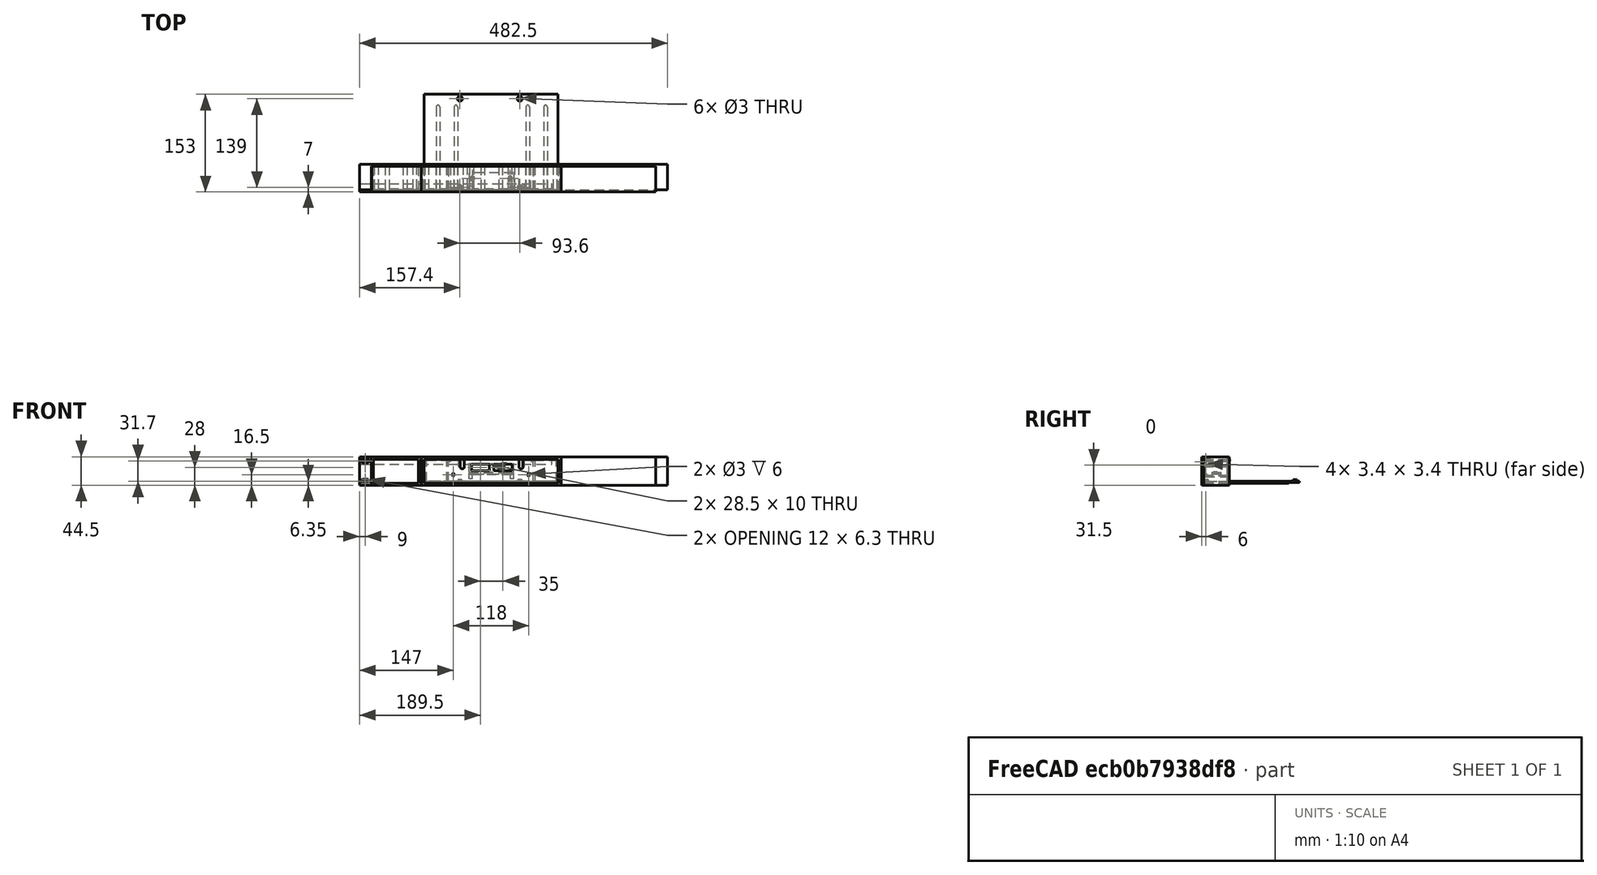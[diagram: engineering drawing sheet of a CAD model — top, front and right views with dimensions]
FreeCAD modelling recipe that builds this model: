
FCSTD DOCUMENT  (FreeCAD 0.19R24291 (Git))
Label: Rack_-_Middle_wider
License: All rights reserved
LicenseURL: http://en.wikipedia.org/wiki/All_rights_reserved
objects: Part::Box×100, Part::MultiFuse×44, Part::Cut×30, Part::Fillet×18, Part::Cylinder×18, Part::Cone×8, Mesh::Feature×7, Part::MultiCommon×6, App::MeasureDistance×1
note: 224 computed .brp shape members not serialized (recipe doc carries the construction recipe); baked Part::Feature solids carry a one-line shape summary decoded from their .brp

FEATURE [Mesh::Feature] Rack___Right_Side  label="Rack - Right Side"
FEATURE [Mesh::Feature] Rack___Middle  label="Rack - Middle"
FEATURE [Mesh::Feature] Rack___Left_Side  label="Rack - Left Side"
FEATURE [Part::Box] Box  label="Cube"
  AttacherType = Attacher::AttachEngine3D
  Height = 10
  Length = 300
  Placement = pos=(1,0,33) rot=(0,0,1;0rad)
  Width = 10
FEATURE [Part::Box] Box001  label="Cube001"
  AttacherType = Attacher::AttachEngine3D
  Height = 44.5
  Length = 445
  Placement = pos=(18.75,-3,0) rot=(0,0,1;0rad)
  Width = 40
FEATURE [Part::Box] Box002  label="Cube002"
  AttacherType = Attacher::AttachEngine3D
  Height = 44.5
  Length = 219.5
  Placement = pos=(96.5,-3,0) rot=(0,0,1;0rad)
  Width = 40
FEATURE [Part::Box] Box003  label="Cube003"
  AttacherType = Attacher::AttachEngine3D
  Height = 44
  Length = 482.5
  Width = 40
FEATURE [Part::Box] Box004  label="Cube004"
  AttacherType = Attacher::AttachEngine3D
  Height = 17.92
  Length = 3
  Placement = pos=(313.75,0,13.25) rot=(0,0,1;0rad)
  Width = 37
FEATURE [Part::Box] Box005  label="Cube005"
  AttacherType = Attacher::AttachEngine3D
  Height = 17.92
  Length = 3
  Placement = pos=(313,0,12.75) rot=(0,1,0;0.959931rad)
  Width = 37
FEATURE [Part::Box] Box006  label="Cube006"
  AttacherType = Attacher::AttachEngine3D
  Height = 17.92
  Length = 3
  Placement = pos=(313,0,35.35) rot=(0,1,0;2.18166rad)
  Width = 37
FEATURE [Part::MultiFuse] Fusion
  Shapes = -> [Box006,Box005]
FEATURE [Part::Cut] Cut
  Base = -> Box004
  Tool = -> Fusion
FEATURE [Part::Box] Box007  label="Cube007"
  AttacherType = Attacher::AttachEngine3D
  Height = 17.92
  Length = 3
  Placement = pos=(314.75,-3,13.25) rot=(0,0,1;0.785398rad)
  Width = 37
FEATURE [Part::Cut] Cut001
  Base = -> Cut
  Tool = -> Box007
FEATURE [Part::Cut] Cut002
  Base = -> Box002
  Tool = -> Cut001
FEATURE [Part::Box] Box008  label="Cube008"
  AttacherType = Attacher::AttachEngine3D
  Height = 17.92
  Length = 3
  Placement = pos=(313,0,12.75) rot=(0,1,0;0.959931rad)
  Width = 37
FEATURE [Part::Box] Box009  label="Cube009"
  AttacherType = Attacher::AttachEngine3D
  Height = 17.92
  Length = 3
  Placement = pos=(313,0,35.35) rot=(0,1,0;2.18166rad)
  Width = 37
FEATURE [Part::MultiFuse] Fusion001
  Shapes = -> [Box009,Box008]
FEATURE [Part::Box] Box010  label="Cube010"
  AttacherType = Attacher::AttachEngine3D
  Height = 17.92
  Length = 3
  Placement = pos=(314.75,-3,13.25) rot=(0,0,1;0.785398rad)
  Width = 37
FEATURE [Part::Box] Box011  label="Cube011"
  AttacherType = Attacher::AttachEngine3D
  Height = 17.92
  Length = 3
  Placement = pos=(313.75,0,13.25) rot=(0,0,1;0rad)
  Width = 37
FEATURE [Part::Cut] Cut003
  Base = -> Box011
  Tool = -> Fusion001
FEATURE [Part::Cut] Cut004
  Base = -> Cut003
  Placement = pos=(413.25,0,44.45) rot=(0,1,0;3.14159rad)
  Tool = -> Box010
FEATURE [Part::Cut] Cut005  label="middle"
  Base = -> Cut002
  Tool = -> Cut004
FEATURE [Part::Box] Box012  label="Cube012"
  AttacherType = Attacher::AttachEngine3D
  Height = 17.92
  Length = 3
  Placement = pos=(313.75,0,13.25) rot=(0,0,1;0rad)
  Width = 37
FEATURE [Part::Box] Box013  label="Cube013"
  AttacherType = Attacher::AttachEngine3D
  Height = 17.92
  Length = 3
  Placement = pos=(314.75,-3,13.25) rot=(0,0,1;0.785398rad)
  Width = 37
FEATURE [Part::Box] Box014  label="Cube014"
  AttacherType = Attacher::AttachEngine3D
  Height = 17.92
  Length = 3
  Placement = pos=(313,0,12.75) rot=(0,1,0;0.959931rad)
  Width = 37
FEATURE [Part::Box] Box015  label="Cube015"
  AttacherType = Attacher::AttachEngine3D
  Height = 17.92
  Length = 3
  Placement = pos=(313,0,35.35) rot=(0,1,0;2.18166rad)
  Width = 37
FEATURE [Part::MultiFuse] Fusion002
  Shapes = -> [Box015,Box014]
FEATURE [Part::Cut] Cut006
  Base = -> Box012
  Tool = -> Fusion002
FEATURE [Part::Cut] Cut007
  Base = -> Cut006
  Placement = pos=(413.25,0,44.45) rot=(0,1,0;3.14159rad)
  Tool = -> Box013
FEATURE [Part::Box] Box016  label="Cube016"
  AttacherType = Attacher::AttachEngine3D
  Height = 44.5
  Length = 96.5
  Placement = pos=(0,-3,0) rot=(0,0,1;0rad)
  Width = 40
FEATURE [Part::MultiFuse] Fusion003
  Shapes = -> [Cut007,Box016]
FEATURE [Part::Box] Box017  label="Cube017"
  AttacherType = Attacher::AttachEngine3D
  Height = 37.95
  Length = 70.5
  Placement = pos=(22,-4,2.75) rot=(0,0,1;0rad)
  Width = 45
FEATURE [Part::Cut] Cut008  label="left"
  Base = -> Fusion003
  Tool = -> Box017
FEATURE [Part::Box] Box018  label="Cube018"
  AttacherType = Attacher::AttachEngine3D
  Height = 45
  Length = 19
  Width = 37
FEATURE [Part::Box] Box019  label="Cube019"
  AttacherType = Attacher::AttachEngine3D
  Height = 6.3
  Length = 12
  Placement = pos=(3,-3,3.2) rot=(0,0,1;0rad)
  Width = 10
FEATURE [Part::Fillet] Fillet
  Base = -> Box019
  Edges = 4 edges r=3: [Edge2,Edge4,Edge6,Edge8]
  Placement = pos=(0,-1,0) rot=(0,0,1;0rad)
FEATURE [Part::Box] Box020  label="Cube020"
  AttacherType = Attacher::AttachEngine3D
  Height = 6.3
  Length = 12
  Placement = pos=(3,-3,3.2) rot=(0,0,1;0rad)
  Width = 10
FEATURE [Part::Fillet] Fillet001
  Base = -> Box020
  Edges = 4 edges r=3: [Edge2,Edge4,Edge6,Edge8]
  Placement = pos=(0,-1,31.7) rot=(0,0,1;0rad)
FEATURE [Part::MultiFuse] Fusion004
  Shapes = -> [Box018,Fillet,Fillet001]
FEATURE [Part::Cut] Cut009
  Base = -> Cut008
  Tool = -> Fusion004
FEATURE [Part::Box] Box021  label="Cube021"
  AttacherType = Attacher::AttachEngine3D
  Height = 4
  Length = 19
  Placement = pos=(22,0,0) rot=(0,0,1;0rad)
  Width = 37
FEATURE [Part::Box] Box022  label="Cube022"
  AttacherType = Attacher::AttachEngine3D
  Height = 4
  Length = 22
  Placement = pos=(47,0,0) rot=(0,0,1;0rad)
  Width = 37
FEATURE [Part::Box] Box023  label="Cube023"
  AttacherType = Attacher::AttachEngine3D
  Height = 4
  Length = 18
  Placement = pos=(75,0,0) rot=(0,0,1;0rad)
  Width = 37
FEATURE [Part::Box] Box024  label="Cube024"
  AttacherType = Attacher::AttachEngine3D
  Height = 4
  Length = 54
  Placement = pos=(30.05,0,39.45) rot=(0,0,1;0rad)
  Width = 37
FEATURE [Part::Box] Box025  label="Cube025"
  AttacherType = Attacher::AttachEngine3D
  Height = 4
  Length = 3
  Placement = pos=(21.05,0,39.45) rot=(0,0,1;0rad)
  Width = 37
FEATURE [Part::Box] Box026  label="Cube026"
  AttacherType = Attacher::AttachEngine3D
  Height = 4
  Length = 4
  Placement = pos=(90.05,0,39.45) rot=(0,0,1;0rad)
  Width = 37
FEATURE [Part::Box] Box027  label="Cube027"
  AttacherType = Attacher::AttachEngine3D
  Height = 10
  Length = 71
  Placement = pos=(22,-3,0) rot=(1,0,0;0.785398rad)
  Width = 10
FEATURE [Part::MultiFuse] Fusion005
  Shapes = -> [Box021,Box022,Box023]
FEATURE [Part::Cut] Cut010
  Base = -> Fusion005
  Tool = -> Box027
FEATURE [Part::MultiFuse] Fusion006
  Shapes = -> [Box024,Box025,Box026]
FEATURE [Part::Box] Box028  label="Cube028"
  AttacherType = Attacher::AttachEngine3D
  Height = 10
  Length = 80
  Placement = pos=(13,-8,35) rot=(1,0,0;-0.785398rad)
  Width = 10
FEATURE [Part::Cut] Cut011
  Base = -> Fusion006
  Tool = -> Box028
FEATURE [Part::MultiFuse] Fusion007  label="Rack - Left Side shorter"
  Shapes = -> [Cut009,Cut010,Cut011]
FEATURE [Part::Box] Box029  label="Cube029"
  AttacherType = Attacher::AttachEngine3D
  Height = 37.95
  Length = 210.4
  Placement = pos=(101,-4,2.75) rot=(0,0,1;0rad)
  Width = 45
FEATURE [Part::Cut] Cut012
  Base = -> Cut005
  Tool = -> Box029
FEATURE [Part::Box] Box030  label="Cube030"
  AttacherType = Attacher::AttachEngine3D
  Height = 4
  Length = 3
  Placement = pos=(21.05,0,39.45) rot=(0,0,1;0rad)
  Width = 37
FEATURE [Part::Box] Box031  label="Cube031"
  AttacherType = Attacher::AttachEngine3D
  Height = 10
  Length = 85
  Placement = pos=(13,-8,35) rot=(-1,0,0;0.785398rad)
  Width = 10
FEATURE [Part::Box] Box032  label="Cube032"
  AttacherType = Attacher::AttachEngine3D
  Height = 4
  Length = 4
  Placement = pos=(90.05,0,39.45) rot=(0,0,1;0rad)
  Width = 37
FEATURE [Part::Box] Box033  label="Cube033"
  AttacherType = Attacher::AttachEngine3D
  Height = 4
  Length = 54
  Placement = pos=(30.05,0,39.45) rot=(0,0,1;0rad)
  Width = 37
FEATURE [Part::MultiFuse] Fusion008
  Shapes = -> [Box033,Box030,Box032]
FEATURE [Part::Cut] Cut013
  Base = -> Fusion008
  Placement = pos=(219.5,0,0) rot=(0,0,1;0rad)
  Tool = -> Box031
FEATURE [Part::Box] Box034  label="Cube034"
  AttacherType = Attacher::AttachEngine3D
  Height = 4
  Length = 4
  Placement = pos=(90.05,0,39.45) rot=(0,0,1;0rad)
  Width = 37
FEATURE [Part::Box] Box035  label="Cube035"
  AttacherType = Attacher::AttachEngine3D
  Height = 10
  Length = 85
  Placement = pos=(13,-8,35) rot=(-1,0,0;0.785398rad)
  Width = 10
FEATURE [Part::Box] Box036  label="Cube036"
  AttacherType = Attacher::AttachEngine3D
  Height = 4
  Length = 54
  Placement = pos=(30.05,0,39.45) rot=(0,0,1;0rad)
  Width = 37
FEATURE [Part::Box] Box037  label="Cube037"
  AttacherType = Attacher::AttachEngine3D
  Height = 4
  Length = 3
  Placement = pos=(21.05,0,39.45) rot=(0,0,1;0rad)
  Width = 37
FEATURE [Part::MultiFuse] Fusion009
  Shapes = -> [Box036,Box037,Box034]
FEATURE [Part::Cut] Cut014
  Base = -> Fusion009
  Placement = pos=(149,0,0) rot=(0,0,1;0rad)
  Tool = -> Box035
FEATURE [Part::Box] Box038  label="Cube038"
  AttacherType = Attacher::AttachEngine3D
  Height = 4
  Length = 4
  Placement = pos=(90.05,0,39.45) rot=(0,0,1;0rad)
  Width = 37
FEATURE [Part::Box] Box039  label="Cube039"
  AttacherType = Attacher::AttachEngine3D
  Height = 10
  Length = 85
  Placement = pos=(13,-8,35) rot=(-1,0,0;0.785398rad)
  Width = 10
FEATURE [Part::Box] Box040  label="Cube040"
  AttacherType = Attacher::AttachEngine3D
  Height = 4
  Length = 54
  Placement = pos=(30.05,0,39.45) rot=(0,0,1;0rad)
  Width = 37
FEATURE [Part::Box] Box041  label="Cube041"
  AttacherType = Attacher::AttachEngine3D
  Height = 4
  Length = 3
  Placement = pos=(21.05,0,39.45) rot=(0,0,1;0rad)
  Width = 37
FEATURE [Part::MultiFuse] Fusion010
  Shapes = -> [Box040,Box041,Box038]
FEATURE [Part::Cut] Cut015
  Base = -> Fusion010
  Placement = pos=(79,0,0) rot=(0,0,1;0rad)
  Tool = -> Box039
FEATURE [Part::Box] Box042  label="Cube042"
  AttacherType = Attacher::AttachEngine3D
  Height = 4
  Length = 18
  Placement = pos=(75,0,0) rot=(0,0,1;0rad)
  Width = 37
FEATURE [Part::Box] Box043  label="Cube043"
  AttacherType = Attacher::AttachEngine3D
  Height = 4
  Length = 19
  Placement = pos=(22,0,0) rot=(0,0,1;0rad)
  Width = 37
FEATURE [Part::Box] Box044  label="Cube044"
  AttacherType = Attacher::AttachEngine3D
  Height = 4
  Length = 22
  Placement = pos=(47,0,0) rot=(0,0,1;0rad)
  Width = 37
FEATURE [Part::MultiFuse] Fusion011
  Shapes = -> [Box043,Box044,Box042]
FEATURE [Part::Box] Box045  label="Cube045"
  AttacherType = Attacher::AttachEngine3D
  Height = 10
  Length = 71
  Placement = pos=(22,-3,0) rot=(1,0,0;0.785398rad)
  Width = 10
FEATURE [Part::Cut] Cut016
  Base = -> Fusion011
  Placement = pos=(219.5,0,0) rot=(0,0,1;0rad)
  Tool = -> Box045
FEATURE [Part::Box] Box046  label="Cube046"
  AttacherType = Attacher::AttachEngine3D
  Height = 4
  Length = 18
  Placement = pos=(75,0,0) rot=(0,0,1;0rad)
  Width = 37
FEATURE [Part::Box] Box047  label="Cube047"
  AttacherType = Attacher::AttachEngine3D
  Height = 4
  Length = 19
  Placement = pos=(22,0,0) rot=(0,0,1;0rad)
  Width = 37
FEATURE [Part::Box] Box048  label="Cube048"
  AttacherType = Attacher::AttachEngine3D
  Height = 4
  Length = 22
  Placement = pos=(47,0,0) rot=(0,0,1;0rad)
  Width = 37
FEATURE [Part::MultiFuse] Fusion012
  Shapes = -> [Box047,Box048,Box046]
FEATURE [Part::Box] Box049  label="Cube049"
  AttacherType = Attacher::AttachEngine3D
  Height = 10
  Length = 71
  Placement = pos=(22,-3,0) rot=(1,0,0;0.785398rad)
  Width = 10
FEATURE [Part::Cut] Cut017
  Base = -> Fusion012
  Placement = pos=(149.5,0,0) rot=(0,0,1;0rad)
  Tool = -> Box049
FEATURE [Part::Box] Box050  label="Cube050"
  AttacherType = Attacher::AttachEngine3D
  Height = 4
  Length = 18
  Placement = pos=(75,0,0) rot=(0,0,1;0rad)
  Width = 37
FEATURE [Part::Box] Box051  label="Cube051"
  AttacherType = Attacher::AttachEngine3D
  Height = 4
  Length = 19
  Placement = pos=(22,0,0) rot=(0,0,1;0rad)
  Width = 37
FEATURE [Part::Box] Box052  label="Cube052"
  AttacherType = Attacher::AttachEngine3D
  Height = 4
  Length = 22
  Placement = pos=(47,0,0) rot=(0,0,1;0rad)
  Width = 37
FEATURE [Part::MultiFuse] Fusion013
  Shapes = -> [Box051,Box052,Box050]
FEATURE [Part::Box] Box053  label="Cube053"
  AttacherType = Attacher::AttachEngine3D
  Height = 10
  Length = 71
  Placement = pos=(22,-3,0) rot=(1,0,0;0.785398rad)
  Width = 10
FEATURE [Part::Cut] Cut018
  Base = -> Fusion013
  Placement = pos=(79,0,0) rot=(0,0,1;0rad)
  Tool = -> Box053
FEATURE [Part::MultiFuse] Fusion014  label="Rack - Middle Wider"
  Shapes = -> [Cut012,Cut013,Cut014,Cut015,Cut016,Cut017,Cut018]
FEATURE [Part::Box] Box054  label="Cube054"
  AttacherType = Attacher::AttachEngine3D
  Height = 2
  Length = 150
  Placement = pos=(0,-56,0) rot=(0,0,1;0rad)
  Width = 209.75
FEATURE [Part::Cylinder] Cylinder
  Angle = 360
  AttacherType = Attacher::AttachEngine3D
  Height = 10
  Placement = pos=(4,4,-1) rot=(0,0,1;0rad)
  Radius = 1.5
FEATURE [Part::Box] Box055  label="Cube055"
  AttacherType = Attacher::AttachEngine3D
  Height = 37.5
  Length = 3
  Placement = pos=(-5,-55,-1) rot=(0,0,1;0rad)
  Width = 209.75
FEATURE [Part::Box] Box056  label="Cube056"
  AttacherType = Attacher::AttachEngine3D
  Height = 3
  Length = 130
  Placement = pos=(0,0,-2) rot=(0,0,1;0rad)
  Width = 5.5
FEATURE [Part::Fillet] Fillet002
  Base = -> Box056
  Edges = 2 edges r=0.5: [Edge9,Edge11]
FEATURE [Part::Cylinder] Cylinder004
  Angle = 360
  AttacherType = Attacher::AttachEngine3D
  Height = 3
  Placement = pos=(130,2.75,-2) rot=(0,0,-1;0rad)
  Radius = 2.75
FEATURE [Part::Fillet] Fillet003
  Base = -> Cylinder004
  Edges = 1 edges r=0.5: [Edge3]
FEATURE [Part::MultiFuse] Fusion015
  Placement = pos=(0,-39.25,1) rot=(0,0,1;0rad)
  Shapes = -> [Fillet002,Fillet003]
FEATURE [Part::Cylinder] Cylinder005
  Angle = 360
  AttacherType = Attacher::AttachEngine3D
  Height = 3
  Placement = pos=(130,2.75,-2) rot=(0,0,-1;0rad)
  Radius = 2.75
FEATURE [Part::Box] Box057  label="Cube057"
  AttacherType = Attacher::AttachEngine3D
  Height = 3
  Length = 130
  Placement = pos=(0,0,-2) rot=(0,0,1;0rad)
  Width = 5.5
FEATURE [Part::Fillet] Fillet004
  Base = -> Box057
  Edges = 2 edges r=0.5: [Edge9,Edge11]
FEATURE [Part::Fillet] Fillet005
  Base = -> Cylinder005
  Edges = 1 edges r=0.5: [Edge3]
FEATURE [Part::MultiFuse] Fusion016
  Placement = pos=(0,129.25,1) rot=(0,0,1;0rad)
  Shapes = -> [Fillet004,Fillet005]
FEATURE [Part::Cylinder] Cylinder006
  Angle = 360
  AttacherType = Attacher::AttachEngine3D
  Height = 3
  Placement = pos=(130,2.75,-2) rot=(0,0,-1;0rad)
  Radius = 2.75
FEATURE [Part::Box] Box058  label="Cube058"
  AttacherType = Attacher::AttachEngine3D
  Height = 3
  Length = 130
  Placement = pos=(0,0,-2) rot=(0,0,1;0rad)
  Width = 5.5
FEATURE [Part::Fillet] Fillet006
  Base = -> Box058
  Edges = 2 edges r=0.5: [Edge9,Edge11]
FEATURE [Part::Fillet] Fillet007
  Base = -> Cylinder006
  Edges = 1 edges r=0.5: [Edge3]
FEATURE [Part::MultiFuse] Fusion017
  Placement = pos=(0,101.25,1) rot=(0,0,1;0rad)
  Shapes = -> [Fillet006,Fillet007]
FEATURE [Part::Cylinder] Cylinder007
  Angle = 360
  AttacherType = Attacher::AttachEngine3D
  Height = 3
  Placement = pos=(130,2.75,-2) rot=(0,0,-1;0rad)
  Radius = 2.75
FEATURE [Part::Box] Box059  label="Cube059"
  AttacherType = Attacher::AttachEngine3D
  Height = 3
  Length = 130
  Placement = pos=(0,0,-2) rot=(0,0,1;0rad)
  Width = 5.5
FEATURE [Part::Fillet] Fillet008
  Base = -> Box059
  Edges = 2 edges r=0.5: [Edge9,Edge11]
FEATURE [Part::Fillet] Fillet009
  Base = -> Cylinder007
  Edges = 1 edges r=0.5: [Edge3]
FEATURE [Part::MultiFuse] Fusion018
  Placement = pos=(0,-11.25,1) rot=(0,0,1;0rad)
  Shapes = -> [Fillet008,Fillet009]
FEATURE [Part::Box] Box060  label="Cube060"
  AttacherType = Attacher::AttachEngine3D
  Height = 35.2
  Length = 40
  Placement = pos=(0,-20,0) rot=(0,0,1;0rad)
  Width = 3
FEATURE [Part::Box] Box061  label="Cube061"
  AttacherType = Attacher::AttachEngine3D
  Height = 35.2
  Length = 40
  Placement = pos=(0,115.5,0) rot=(0,0,1;0rad)
  Width = 3
FEATURE [Part::Cylinder] Cylinder008
  Angle = 360
  AttacherType = Attacher::AttachEngine3D
  Height = 3
  Placement = pos=(38,2.5,-2) rot=(0,0,-1;0rad)
  Radius = 2.5
FEATURE [Part::Box] Box062  label="Cube062"
  AttacherType = Attacher::AttachEngine3D
  Height = 3
  Length = 38
  Placement = pos=(0,0,-2) rot=(0,0,1;0rad)
  Width = 5
FEATURE [Part::Fillet] Fillet010
  Base = -> Box062
  Edges = 2 edges r=0.5: [Edge9,Edge11]
FEATURE [Part::Fillet] Fillet011
  Base = -> Cylinder008
  Edges = 1 edges r=0.5: [Edge3]
FEATURE [Part::MultiFuse] Fusion019
  Placement = pos=(0,-18.5,35.5) rot=(0,0,1;0rad)
  Shapes = -> [Fillet010,Fillet011]
FEATURE [Part::Cylinder] Cylinder009
  Angle = 360
  AttacherType = Attacher::AttachEngine3D
  Height = 3
  Placement = pos=(38,2.5,-2) rot=(0,0,-1;0rad)
  Radius = 2.5
FEATURE [Part::Box] Box063  label="Cube063"
  AttacherType = Attacher::AttachEngine3D
  Height = 3
  Length = 38
  Placement = pos=(0,0,-2) rot=(0,0,1;0rad)
  Width = 5
FEATURE [Part::Fillet] Fillet012
  Base = -> Box063
  Edges = 2 edges r=0.5: [Edge9,Edge11]
FEATURE [Part::Fillet] Fillet013
  Base = -> Cylinder009
  Edges = 1 edges r=0.5: [Edge3]
FEATURE [Part::MultiFuse] Fusion020
  Placement = pos=(0,112,35.5) rot=(0,0,1;0rad)
  Shapes = -> [Fillet012,Fillet013]
FEATURE [Part::Box] Box064  label="Cube064"
  AttacherType = Attacher::AttachEngine3D
  Height = 5
  Length = 5.45
  Placement = pos=(3.25,0,0) rot=(0,0,1;0rad)
  Width = 10
FEATURE [Part::Box] Box065  label="Cube065"
  AttacherType = Attacher::AttachEngine3D
  Height = 5
  Length = 5.45
  Placement = pos=(11.5,4,0) rot=(0,0,1;2.0944rad)
  Width = 10
FEATURE [Part::Box] Box066  label="Cube066"
  AttacherType = Attacher::AttachEngine3D
  Height = 5
  Length = 10
  Placement = pos=(0.55,4,0) rot=(0,0,-1;0.523599rad)
  Width = 5.45
FEATURE [Part::MultiCommon] Common  label="M.25 nut"
  Placement = pos=(-2,0,-1) rot=(0,0,1;0rad)
  Shapes = -> [Box064,Box066,Box065]
FEATURE [Part::Cone] Cone
  Angle = 360
  AttacherType = Attacher::AttachEngine3D
  Height = 3
  Placement = pos=(4,4,2) rot=(0,0,1;0rad)
  Radius1 = 4
  Radius2 = 3
FEATURE [Part::Cone] Cone001
  Angle = 360
  AttacherType = Attacher::AttachEngine3D
  Height = 3
  Placement = pos=(143,4,2) rot=(0,0,1;0rad)
  Radius1 = 4
  Radius2 = 3
FEATURE [Part::Cone] Cone002
  Angle = 360
  AttacherType = Attacher::AttachEngine3D
  Height = 3
  Placement = pos=(4,97.6,2) rot=(0,0,1;0rad)
  Radius1 = 4
  Radius2 = 3
FEATURE [Part::Cone] Cone003
  Angle = 360
  AttacherType = Attacher::AttachEngine3D
  Height = 3
  Placement = pos=(143,97.6,2) rot=(0,0,1;0rad)
  Radius1 = 4
  Radius2 = 3
FEATURE [Part::Box] Box067  label="Cube067"
  AttacherType = Attacher::AttachEngine3D
  Height = 33.5
  Length = 4
  Placement = pos=(-3,-52,2) rot=(0,0,1;0rad)
  Width = 203
FEATURE [Part::Cut] Cut019  label="Face_plate_full"
  Base = -> Box055
  Placement = pos=(2,0,0) rot=(0,0,1;0rad)
  Tool = -> Box067
FEATURE [Part::Box] Box068  label="Cube068"
  AttacherType = Attacher::AttachEngine3D
  Height = 15
  Length = 10
  Placement = pos=(0,0,16) rot=(0,0,1;0rad)
  Width = 6
FEATURE [Part::Fillet] Fillet014
  Base = -> Box068
  Edges = 2 edges r=2: [Edge9,Edge11]
  Placement = pos=(0,0,4) rot=(0,0,1;0rad)
FEATURE [Part::Box] Box069  label="Cube069"
  AttacherType = Attacher::AttachEngine3D
  Height = 15
  Length = 10
  Placement = pos=(0,0,16) rot=(0,0,1;0rad)
  Width = 6
FEATURE [Part::Fillet] Fillet015
  Base = -> Box069
  Edges = 2 edges r=2: [Edge9,Edge11]
  Placement = pos=(0,92,4) rot=(0,0,1;0rad)
FEATURE [Part::MultiFuse] Fusion021
  Placement = pos=(-5,0,2) rot=(0,0,1;0rad)
  Shapes = -> [Fillet014,Fillet015]
FEATURE [Part::Cut] Cut020  label="Face plate with cuts"
  Base = -> Cut019
  Placement = pos=(0,-1,0) rot=(0,0,1;0rad)
  Tool = -> Fusion021
FEATURE [Part::MultiFuse] Fusion022  label="Bottom"
  Shapes = -> [Box054,Fusion015,Fusion016,Fusion017,Fusion018,Cone,Cone001,Cone002,Cone003]
FEATURE [Part::MultiFuse] Fusion023  label="screw_hole"
  Shapes = -> [Cylinder,Common]
FEATURE [Part::Box] Box070  label="Cube070"
  AttacherType = Attacher::AttachEngine3D
  Height = 5
  Length = 5.45
  Placement = pos=(3.25,0,0) rot=(0,0,1;0rad)
  Width = 10
FEATURE [Part::Box] Box071  label="Cube071"
  AttacherType = Attacher::AttachEngine3D
  Height = 5
  Length = 5.45
  Placement = pos=(11.5,4,0) rot=(0,0,1;2.0944rad)
  Width = 10
FEATURE [Part::Box] Box072  label="Cube072"
  AttacherType = Attacher::AttachEngine3D
  Height = 5
  Length = 10
  Placement = pos=(0.55,4,0) rot=(0,0,-1;0.523599rad)
  Width = 5.45
FEATURE [Part::Cylinder] Cylinder010
  Angle = 360
  AttacherType = Attacher::AttachEngine3D
  Height = 10
  Placement = pos=(4,4,-1) rot=(0,0,1;0rad)
  Radius = 1.5
FEATURE [Part::MultiCommon] Common001  label="M.25 nut001"
  Placement = pos=(-2,0,-1) rot=(0,0,1;0rad)
  Shapes = -> [Box070,Box072,Box071]
FEATURE [Part::MultiFuse] Fusion024  label="screw_hole001"
  Placement = pos=(139,0,0) rot=(0,0,1;0rad)
  Shapes = -> [Cylinder010,Common001]
FEATURE [Part::Box] Box073  label="Cube073"
  AttacherType = Attacher::AttachEngine3D
  Height = 5
  Length = 5.45
  Placement = pos=(3.25,0,0) rot=(0,0,1;0rad)
  Width = 10
FEATURE [Part::Box] Box074  label="Cube074"
  AttacherType = Attacher::AttachEngine3D
  Height = 5
  Length = 5.45
  Placement = pos=(11.5,4,0) rot=(0,0,1;2.0944rad)
  Width = 10
FEATURE [Part::Box] Box075  label="Cube075"
  AttacherType = Attacher::AttachEngine3D
  Height = 5
  Length = 10
  Placement = pos=(0.55,4,0) rot=(0,0,-1;0.523599rad)
  Width = 5.45
FEATURE [Part::Cylinder] Cylinder011
  Angle = 360
  AttacherType = Attacher::AttachEngine3D
  Height = 10
  Placement = pos=(4,4,-1) rot=(0,0,1;0rad)
  Radius = 1.5
FEATURE [Part::MultiCommon] Common002  label="M.25 nut002"
  Placement = pos=(-2,0,-1) rot=(0,0,1;0rad)
  Shapes = -> [Box073,Box075,Box074]
FEATURE [Part::MultiFuse] Fusion025  label="screw_hole002"
  Placement = pos=(0,93.6,0) rot=(0,0,1;0rad)
  Shapes = -> [Cylinder011,Common002]
FEATURE [Part::Box] Box076  label="Cube076"
  AttacherType = Attacher::AttachEngine3D
  Height = 5
  Length = 5.45
  Placement = pos=(3.25,0,0) rot=(0,0,1;0rad)
  Width = 10
FEATURE [Part::Box] Box077  label="Cube077"
  AttacherType = Attacher::AttachEngine3D
  Height = 5
  Length = 5.45
  Placement = pos=(11.5,4,0) rot=(0,0,1;2.0944rad)
  Width = 10
FEATURE [Part::Box] Box078  label="Cube078"
  AttacherType = Attacher::AttachEngine3D
  Height = 5
  Length = 10
  Placement = pos=(0.55,4,0) rot=(0,0,-1;0.523599rad)
  Width = 5.45
FEATURE [Part::Cylinder] Cylinder012
  Angle = 360
  AttacherType = Attacher::AttachEngine3D
  Height = 10
  Placement = pos=(4,4,-1) rot=(0,0,1;0rad)
  Radius = 1.5
FEATURE [Part::MultiCommon] Common003  label="M.25 nut003"
  Placement = pos=(-2,0,-1) rot=(0,0,1;0rad)
  Shapes = -> [Box076,Box078,Box077]
FEATURE [Part::MultiFuse] Fusion026  label="screw_hole003"
  Placement = pos=(139,93.6,0) rot=(0,0,1;0rad)
  Shapes = -> [Cylinder012,Common003]
FEATURE [Part::MultiFuse] Fusion027  label="Screws"
  Placement = pos=(0,0,-1.5) rot=(0,0,1;0rad)
  Shapes = -> [Fusion023,Fusion024,Fusion025,Fusion026]
FEATURE [Part::MultiFuse] Fusion028  label="SBC61_tray_whole"
  Shapes = -> [Fusion019,Fusion020,Box061,Box060,Cut020]
FEATURE [Part::Cylinder] Cylinder003
  Angle = 360
  AttacherType = Attacher::AttachEngine3D
  Height = 10
  Placement = pos=(63,5,7) rot=(1,0,0;1.5708rad)
  Radius = 1.5
FEATURE [Part::Cylinder] Cylinder002
  Angle = 360
  AttacherType = Attacher::AttachEngine3D
  Height = 10
  Placement = pos=(38,5,7) rot=(1,0,0;1.5708rad)
  Radius = 1.5
FEATURE [Part::Cylinder] Cylinder001
  Angle = 360
  AttacherType = Attacher::AttachEngine3D
  Height = 10
  Placement = pos=(28,5,7) rot=(1,0,0;1.5708rad)
  Radius = 1.5
FEATURE [Part::Box] Box079  label="Cube079"
  AttacherType = Attacher::AttachEngine3D
  Height = 10
  Length = 28.5
  Placement = pos=(1.25,-1,2) rot=(0,0,1;0rad)
  Width = 10
FEATURE [Part::Cylinder] Cylinder013
  Angle = 360
  AttacherType = Attacher::AttachEngine3D
  Height = 10
  Placement = pos=(3,5,7) rot=(1,0,0;1.5708rad)
  Radius = 1.5
FEATURE [Part::Box] Box080  label="Cube080"
  AttacherType = Attacher::AttachEngine3D
  Height = 10
  Length = 28.5
  Placement = pos=(36.25,-1,2) rot=(0,0,1;0rad)
  Width = 10
FEATURE [Part::MultiFuse] Fusion030
  Shapes = -> [Cylinder013,Cylinder001,Cylinder002,Cylinder003]
FEATURE [Part::Box] Box081  label="Cube081"
  AttacherType = Attacher::AttachEngine3D
  Height = 13
  Length = 70
  Placement = pos=(-1.5,0,0) rot=(0,0,1;0rad)
  Width = 5
FEATURE [Part::MultiFuse] Fusion029
  Placement = pos=(3,15,17) rot=(0,0,1;1.5708rad)
  Shapes = -> [Cylinder003,Fusion030,Cylinder001,Cylinder002,Box081,Cylinder013,Box079,Box080]
FEATURE [Part::Cut] Cut021
  Base = -> Fusion028
  Tool = -> Fusion029
FEATURE [Part::Box] Box082  label="Cube082"
  AttacherType = Attacher::AttachEngine3D
  Height = 2.5
  Length = 70
  Placement = pos=(26.5,13.5,13) rot=(0,0,1;1.5708rad)
  Width = 30
FEATURE [Part::Cone] Cone004
  Angle = 360
  AttacherType = Attacher::AttachEngine3D
  Height = 3
  Placement = pos=(17.5,19,14) rot=(0,0,1;0rad)
  Radius1 = 4
  Radius2 = 3
FEATURE [Part::Cone] Cone005
  Angle = 360
  AttacherType = Attacher::AttachEngine3D
  Height = 3
  Placement = pos=(17.5,78,14) rot=(0,0,1;0rad)
  Radius1 = 4
  Radius2 = 3
FEATURE [Part::Box] Box083  label="Cube083"
  AttacherType = Attacher::AttachEngine3D
  Height = 10
  Length = 10
  Width = 5
FEATURE [Part::Box] Box084  label="Cube084"
  AttacherType = Attacher::AttachEngine3D
  Height = 20
  Length = 10
  Placement = pos=(0,0,0) rot=(0,1,0;0.785398rad)
  Width = 5
FEATURE [Part::Cut] Cut022
  Base = -> Box083
  Placement = pos=(-3.5,13.5,4) rot=(0,0,1;0rad)
  Tool = -> Box084
FEATURE [Part::Box] Box085  label="Cube085"
  AttacherType = Attacher::AttachEngine3D
  Height = 20
  Length = 10
  Placement = pos=(0,0,0) rot=(0,1,0;0.785398rad)
  Width = 5
FEATURE [Part::Box] Box086  label="Cube086"
  AttacherType = Attacher::AttachEngine3D
  Height = 10
  Length = 10
  Width = 5
FEATURE [Part::Cut] Cut023  label="Cut005"
  Base = -> Box086
  Placement = pos=(-3.5,78.5,4) rot=(0,0,1;0rad)
  Tool = -> Box085
FEATURE [Part::MultiFuse] Fusion031  label="CS863 board"
  Shapes = -> [Box082,Cone004,Cone005,Cut022,Cut023]
FEATURE [Part::Box] Box087  label="Cube087"
  AttacherType = Attacher::AttachEngine3D
  Height = 2
  Length = 5.45
  Placement = pos=(3.25,0,0) rot=(0,0,1;0rad)
  Width = 10
FEATURE [Part::Box] Box088  label="Cube088"
  AttacherType = Attacher::AttachEngine3D
  Height = 2
  Length = 5.45
  Placement = pos=(11.5,4,0) rot=(0,0,1;2.0944rad)
  Width = 10
FEATURE [Part::Box] Box089  label="Cube089"
  AttacherType = Attacher::AttachEngine3D
  Height = 2
  Length = 10
  Placement = pos=(0.55,4,0) rot=(0,0,-1;0.523599rad)
  Width = 5.45
FEATURE [Part::Cylinder] Cylinder014
  Angle = 360
  AttacherType = Attacher::AttachEngine3D
  Height = 10
  Placement = pos=(4,4,-1) rot=(0,0,1;0rad)
  Radius = 1.5
FEATURE [Part::MultiCommon] Common004  label="M.25 nut004"
  Placement = pos=(-2,0,-1) rot=(0,0,1;0rad)
  Shapes = -> [Box087,Box089,Box088]
FEATURE [Part::MultiFuse] Fusion032  label="screw_hole004"
  Placement = pos=(13.5,15,13) rot=(0,0,1;0rad)
  Shapes = -> [Cylinder014,Common004]
FEATURE [Part::Box] Box090  label="Cube090"
  AttacherType = Attacher::AttachEngine3D
  Height = 2
  Length = 10
  Placement = pos=(0.55,4,0) rot=(0,0,-1;0.523599rad)
  Width = 5.45
FEATURE [Part::Cylinder] Cylinder015
  Angle = 360
  AttacherType = Attacher::AttachEngine3D
  Height = 10
  Placement = pos=(4,4,-1) rot=(0,0,1;0rad)
  Radius = 1.5
FEATURE [Part::Box] Box091  label="Cube091"
  AttacherType = Attacher::AttachEngine3D
  Height = 2
  Length = 5.45
  Placement = pos=(3.25,0,0) rot=(0,0,1;0rad)
  Width = 10
FEATURE [Part::Box] Box092  label="Cube092"
  AttacherType = Attacher::AttachEngine3D
  Height = 2
  Length = 5.45
  Placement = pos=(11.5,4,0) rot=(0,0,1;2.0944rad)
  Width = 10
FEATURE [Part::MultiCommon] Common005  label="M.25 nut005"
  Placement = pos=(-2,0,-1) rot=(0,0,1;0rad)
  Shapes = -> [Box091,Box090,Box092]
FEATURE [Part::MultiFuse] Fusion033  label="screw_hole005"
  Placement = pos=(13.5,74,13) rot=(0,0,1;0rad)
  Shapes = -> [Cylinder015,Common005]
FEATURE [Part::MultiFuse] Fusion034  label="CS863 screws"
  Shapes = -> [Fusion032,Fusion033]
FEATURE [Part::Cut] Cut024  label="CS863 support"
  Base = -> Fusion031
  Placement = pos=(0.5,0,0) rot=(0,0,1;0rad)
  Tool = -> Fusion034
FEATURE [Part::Box] Box093  label="Actual C61 board"
  AttacherType = Attacher::AttachEngine3D
  Height = 2
  Length = 147
  Placement = pos=(0,0,5) rot=(0,0,1;0rad)
  Width = 102
FEATURE [Part::MultiFuse] Fusion035
  Shapes = -> [Cut021,Cut024]
FEATURE [Part::Cut] Cut025  label="C61 tray"
  Base = -> Fusion035
  Tool = -> Box093
FEATURE [Part::Cut] Cut026  label="Cut008"
  Base = -> Fusion022
  Tool = -> Fusion027
FEATURE [Part::MultiFuse] Fusion036  label="SBC61 tray whole"
  Shapes = -> [Cut025,Cut026]
FEATURE [Part::Cone] Cone006
  Angle = 360
  AttacherType = Attacher::AttachEngine3D
  Height = 5
  Placement = pos=(-1,-10,32.5) rot=(0,1,0;1.5708rad)
  Radius1 = 3
  Radius2 = 2
FEATURE [Part::Cone] Cone007
  Angle = 360
  AttacherType = Attacher::AttachEngine3D
  Height = 5
  Placement = pos=(-1,108,32.5) rot=(0,1,0;1.5708rad)
  Radius1 = 3
  Radius2 = 2
FEATURE [Part::MultiFuse] Fusion037  label="Fusion022"
  Placement = pos=(-1,0,-20) rot=(0,0,1;0rad)
  Shapes = -> [Cone006,Cone007]
  expr: .Placement.Base.z = -20
FEATURE [Part::Cylinder] Cylinder016
  Angle = 360
  AttacherType = Attacher::AttachEngine3D
  Height = 10
  Placement = pos=(-5,-10,32.5) rot=(0,1,0;1.5708rad)
  Radius = 1.5
FEATURE [Part::Cylinder] Cylinder017
  Angle = 360
  AttacherType = Attacher::AttachEngine3D
  Height = 10
  Placement = pos=(-5,108,32.5) rot=(0,1,0;1.5708rad)
  Radius = 1.5
FEATURE [Part::MultiFuse] Fusion038  label="Fusion023"
  Placement = pos=(0,0,-20) rot=(0,0,1;0rad)
  Shapes = -> [Cylinder016,Cylinder017]
FEATURE [Part::MultiFuse] Fusion039  label="Fusion024"
  Shapes = -> [Fusion036,Fusion037]
FEATURE [Part::Cut] Cut027  label="Tray_fina"
  Base = -> Fusion039
  Tool = -> Fusion038
FEATURE [Part::Box] Box094  label="Cube093"
  AttacherType = Attacher::AttachEngine3D
  Height = 10
  Length = 10
  Placement = pos=(0,10,26) rot=(0,0,1;0rad)
  Width = 3
FEATURE [Part::Box] Box095  label="Cube094"
  AttacherType = Attacher::AttachEngine3D
  Height = 3
  Length = 3
  Placement = pos=(3,10,27) rot=(0,0,1;0rad)
  Width = 3
FEATURE [Part::Box] Box096  label="Cube095"
  AttacherType = Attacher::AttachEngine3D
  Height = 3
  Length = 3
  Placement = pos=(3,10,32) rot=(0,0,1;0rad)
  Width = 3
FEATURE [Part::MultiFuse] Fusion040  label="Fusion025"
  Shapes = -> [Box095,Box096]
FEATURE [Part::Cut] Cut028
  Base = -> Box094
  Tool = -> Fusion040
FEATURE [Part::Fillet] Fillet022  label="zip ties holder"
  Base = -> Cut028
  Edges = 22 edges r=0.2: [Edge5,Edge6,Edge7,Edge8,Edge9,Edge10,Edge11,Edge12,Edge13,Edge14,Edge15,Edge16,Edge19,Edge20,Edge21,Edge22,Edge23,Edge24,Edge25,Edge26,Edge27,Edge28]
  Placement = pos=(-1,-13,-1) rot=(0,0,1;0rad)
FEATURE [Part::Box] Box097  label="Cube096"
  AttacherType = Attacher::AttachEngine3D
  Height = 10
  Length = 10
  Placement = pos=(0,10,26) rot=(0,0,1;0rad)
  Width = 3
FEATURE [Part::Box] Box098  label="Cube097"
  AttacherType = Attacher::AttachEngine3D
  Height = 3
  Length = 3
  Placement = pos=(3,10,27) rot=(0,0,1;0rad)
  Width = 3
FEATURE [Part::Box] Box099  label="Cube098"
  AttacherType = Attacher::AttachEngine3D
  Height = 3
  Length = 3
  Placement = pos=(3,10,32) rot=(0,0,1;0rad)
  Width = 3
FEATURE [Part::MultiFuse] Fusion041  label="Fusion026"
  Shapes = -> [Box098,Box099]
FEATURE [Part::Cut] Cut029
  Base = -> Box097
  Tool = -> Fusion041
FEATURE [Part::Fillet] Fillet023  label="zip ties holder001"
  Base = -> Cut029
  Edges = 22 edges r=0.2: [Edge5,Edge6,Edge7,Edge8,Edge9,Edge10,Edge11,Edge12,Edge13,Edge14,Edge15,Edge16,Edge19,Edge20,Edge21,Edge22,Edge23,Edge24,Edge25,Edge26,Edge27,Edge28]
  Placement = pos=(-1,87,-1) rot=(0,0,1;0rad)
FEATURE [Part::MultiFuse] Fusion042  label="zip ties holders"
  Placement = pos=(-0.5,0,0) rot=(0,0,1;0rad)
  Shapes = -> [Fillet022,Fillet023]
FEATURE [Part::MultiFuse] Fusion043  label="C61 tray - incomplete"
  Placement = pos=(255,0,4) rot=(0,0,1;1.5708rad)
  Shapes = -> [Cut027,Fusion042]
FEATURE [Mesh::Feature] Tray___Pi4___with_HDDs____button_OLED__2_  label="Tray - Pi4 - with HDDs  - button-OLED (2)"
  Placement = pos=(149.5,90,-0.5) rot=(0,0,1;0rad)
FEATURE [Mesh::Feature] Tray___Pi4___button  label="Tray - Pi4 - button"
  Placement = pos=(9,80,0) rot=(0,0,1;0rad)
FEATURE [Mesh::Feature] Tray___Pi4___with_HDDs____button_OLED__2_001  label="Tray - Pi4 - with HDDs  - button-OLED (2)001"
  Placement = pos=(79,83,-0.5) rot=(0,0,1;0rad)
FEATURE [Mesh::Feature] Tray___Pi4___button001  label="Tray - Pi4 - button001"
  Placement = pos=(149.5,80,0) rot=(0,0,1;0rad)
FEATURE [App::MeasureDistance] Distance  label="Distance: 210,40 mm"
  Distance = 210.401
  P1 = (101,-3,20.9662)
  P2 = (311.4,-3,20.3467)
